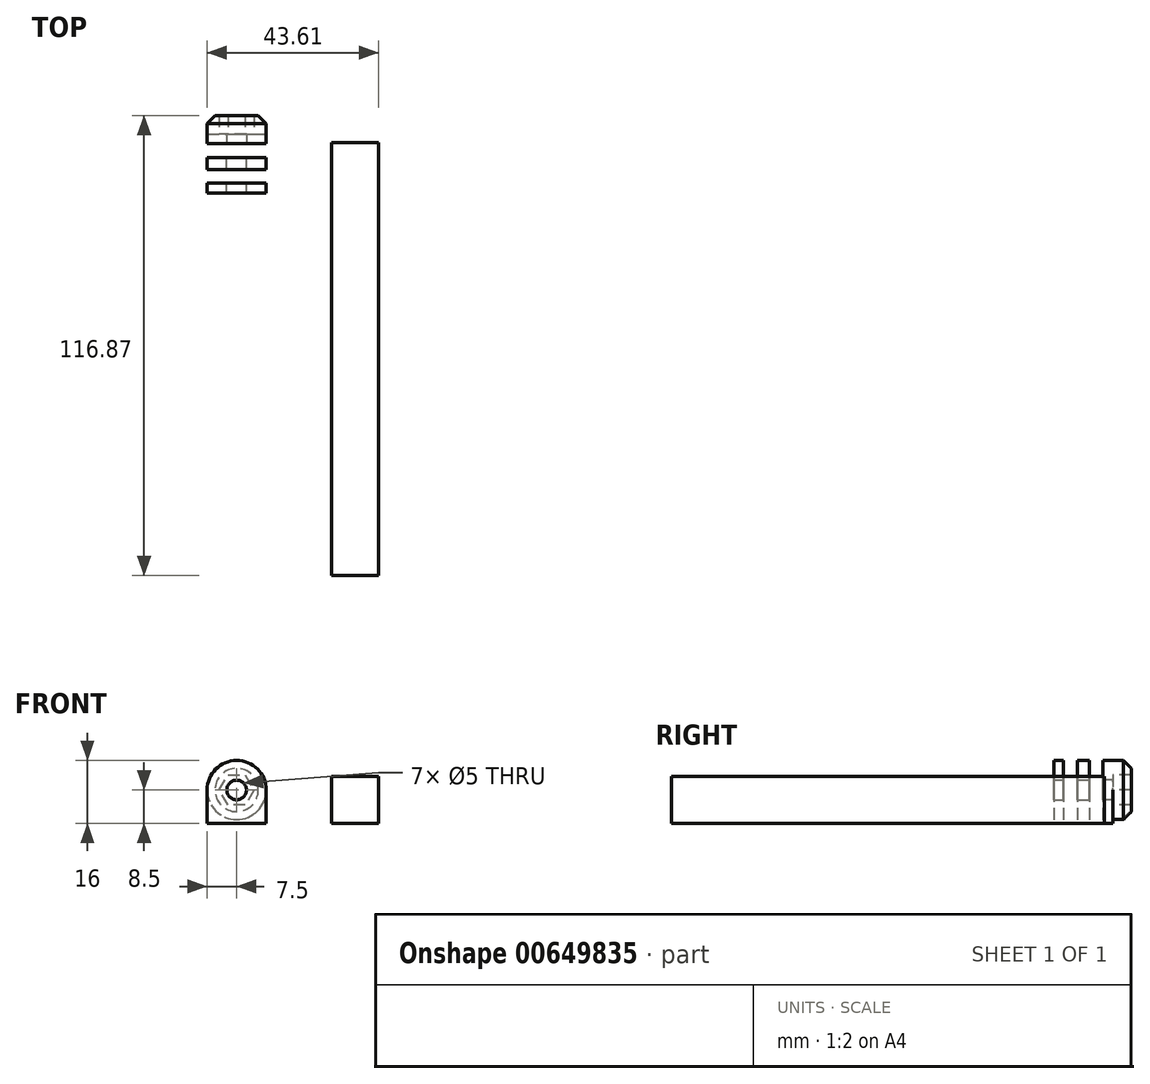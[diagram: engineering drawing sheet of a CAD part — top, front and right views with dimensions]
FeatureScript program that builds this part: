
annotation { "Feature Type Name" : "Feature", "Feature Type Description" : "" }
export const myFeature = defineFeature(function(context is Context, id is Id, definition is map)
    precondition{}
    {
        {
            var Q0;
            Q0=qCreatedBy(makeId("Front.planeOp"),FACE);
            var sketch = newSketch(context, id + "F0", { "sketchPlane" : qUnion([Q0])});
            skCircle(sketch, "E0", {"center": v(0, 0) * mm, "radius": 2.5 * mm});
            skCircle(sketch, "E1", {"center": v(0, 0) * mm, "radius": 7.5 * mm});
            skLineSegment(sketch, "E2", {"start": v(-7.5, 0) * mm, "end": v(-7.5, -8.5) * mm});
            skLineSegment(sketch, "E3", {"start": v(-7.5, -8.5) * mm, "end": v(7.5, -8.5) * mm});
            skLineSegment(sketch, "E4", {"start": v(7.5, 0) * mm, "end": v(7.5, -8.5) * mm});
            skCircle(sketch, "E5.cCircle", {"center": v(0, 0) * mm, "radius": 3.8 * mm, "construction": true});
            skLineSegment(sketch, "E5.0", {"start": v(4.4, 0) * mm, "end": v(2.2, -3.8) * mm});
            skLineSegment(sketch, "E5.1", {"start": v(2.2, -3.8) * mm, "end": v(-2.2, -3.8) * mm});
            skLineSegment(sketch, "E5.2", {"start": v(-2.2, -3.8) * mm, "end": v(-4.4, 0) * mm});
            skLineSegment(sketch, "E5.3", {"start": v(-4.4, 0) * mm, "end": v(-2.2, 3.8) * mm});
            skLineSegment(sketch, "E5.4", {"start": v(-2.2, 3.8) * mm, "end": v(2.2, 3.8) * mm});
            skLineSegment(sketch, "E5.5", {"start": v(2.2, 3.8) * mm, "end": v(4.4, 0) * mm});
            skPoint(sketch, "E5.0.midPoint", {"position": v(3.3, -1.9) * mm});
            skSolve(sketch);
        }
        {
            var Q0;
            {var subQ0=sQuery(id+"F0.wireOp",EDGE,"E2");Q0=makeQuery(id+"F0.imprint","IMPRINT",FACE,{"disambiguationData":[TD([[makeQuery(id+"F0.imprint","IMPRINT",EDGE,{"derivedFrom":subQ0}),1.0]])]});}
            var Q1;
            Q1=makeQuery(id+"F0.imprint","IMPRINT",FACE,{"disambiguationData":[TD([[makeQuery(id+"F0.imprint","IMPRINT",EDGE,{"derivedFrom":sQuery(id+"F0.wireOp",EDGE,"E5.0")}),1.0]])]});
            var Q2;
            Q2=makeQuery(id+"F0.imprint","IMPRINT",FACE,{"disambiguationData":[TD([[makeQuery(id+"F0.imprint","IMPRINT",EDGE,{"derivedFrom":sQuery(id+"F0.wireOp",EDGE,"E0")}),-1.0]])]});
            extrude(context, id + "F1", {"entities" : qUnion([Q0, Q1, Q2]), "endBound" : BoundingType.SYMMETRIC, "depth" : 3 * mm});
        }
        {
            var Q0;
            {var subQ0=sQuery(id+"F0.wireOp",EDGE,"E2");Q0=makeQuery(id+"F0.imprint","IMPRINT",FACE,{"disambiguationData":[TD([[makeQuery(id+"F0.imprint","IMPRINT",EDGE,{"derivedFrom":subQ0}),1.0]])]});}
            var Q1;
            Q1=makeQuery(id+"F0.imprint","IMPRINT",FACE,{"disambiguationData":[TD([[makeQuery(id+"F0.imprint","IMPRINT",EDGE,{"derivedFrom":sQuery(id+"F0.wireOp",EDGE,"E5.0")}),1.0]])]});
            var Q2;
            Q2=makeQuery(id+"F0.imprint","IMPRINT",FACE,{"disambiguationData":[TD([[makeQuery(id+"F0.imprint","IMPRINT",EDGE,{"derivedFrom":sQuery(id+"F0.wireOp",EDGE,"E0")}),-1.0]])]});
            extrude(context, id + "F2", {"entities" : qUnion([Q0, Q1, Q2]), "depth" : 7.5 * mm, "hasSecondDirection" : true, "secondDirectionOppositeDirection" : false, "secondDirectionDepth" : 5 * mm});
        }
        {
            var Q0;
            Q0=makeQuery(id+"F0.imprint","IMPRINT",FACE,{"disambiguationData":[TD([[makeQuery(id+"F0.imprint","IMPRINT",EDGE,{"derivedFrom":sQuery(id+"F0.wireOp",EDGE,"E5.0")}),1.0]])]});
            var Q1;
            {var subQ0=sQuery(id+"F0.wireOp",EDGE,"E2");Q1=makeQuery(id+"F0.imprint","IMPRINT",FACE,{"disambiguationData":[TD([[makeQuery(id+"F0.imprint","IMPRINT",EDGE,{"derivedFrom":subQ0}),1.0]])]});}
            var Q2;
            Q2=makeQuery(id+"F0.imprint","IMPRINT",FACE,{"disambiguationData":[TD([[makeQuery(id+"F0.imprint","IMPRINT",EDGE,{"derivedFrom":sQuery(id+"F0.wireOp",EDGE,"E0")}),-1.0]])]});
            extrude(context, id + "F3", {"entities" : qUnion([Q0, Q1, Q2]), "oppositeDirection" : true, "depth" : 7.5 * mm, "hasSecondDirection" : true, "secondDirectionOppositeDirection" : true, "secondDirectionDepth" : 5 * mm});
        }
        {
            var Q0;
            Q0=makeQuery(id+"F0.imprint","IMPRINT",FACE,{"disambiguationData":[TD([[makeQuery(id+"F0.imprint","IMPRINT",EDGE,{"derivedFrom":sQuery(id+"F0.wireOp",EDGE,"E5.0")}),1.0]])]});
            extrude(context, id + "F4", {"entities" : qUnion([Q0]), "operationType" : NewBodyOperationType.ADD, "oppositeDirection" : true, "depth" : 12.2 * mm, "hasSecondDirection" : true, "secondDirectionOppositeDirection" : true, "secondDirectionDepth" : 7.5 * mm});
        }
        {
            var Q0;
            Q0=makeQuery(id+"F4.opExtrude","CAP_EDGE",EDGE,{"disambiguationData":[OSD([sQuery(id+"F0.wireOp",EDGE,"E1")])],"isStart":false});
            chamfer(context, id + "F5", {"entities" : qUnion([Q0]), "width" : 2 * mm, "tangentPropagation" : true});
        }
        {
            var Q0;
            Q0=makeQuery(id+"F1.opExtrude","SWEPT_FACE",FACE,{"disambiguationData":[OSD([sQuery(id+"F0.wireOp",EDGE,"E3")])]});
            var sketch = newSketch(context, id + "F6", { "sketchPlane" : qUnion([Q0])});
            skLineSegment(sketch, "E6.bottom", {"start": v(36.11, -5.33) * mm, "end": v(24.11, -5.33) * mm});
            skLineSegment(sketch, "E6.top", {"start": v(36.11, 104.67) * mm, "end": v(24.11, 104.67) * mm});
            skLineSegment(sketch, "E6.left", {"start": v(36.11, -5.33) * mm, "end": v(36.11, 104.67) * mm});
            skLineSegment(sketch, "E6.right", {"start": v(24.11, -5.33) * mm, "end": v(24.11, 104.67) * mm});
            skSolve(sketch);
        }
        {
            var Q0;
            Q0=makeQuery(id+"F6.imprint","IMPRINT",FACE,{"disambiguationData":[TD([[makeQuery(id+"F6.imprint","IMPRINT",EDGE,{"derivedFrom":sQuery(id+"F6.wireOp",EDGE,"E6.bottom")}),-1.0]])]});
            extrude(context, id + "F7", {"entities" : qUnion([Q0]), "oppositeDirection" : true, "depth" : 12 * mm, "offsetDistance" : 25 * mm});
        }
    });
